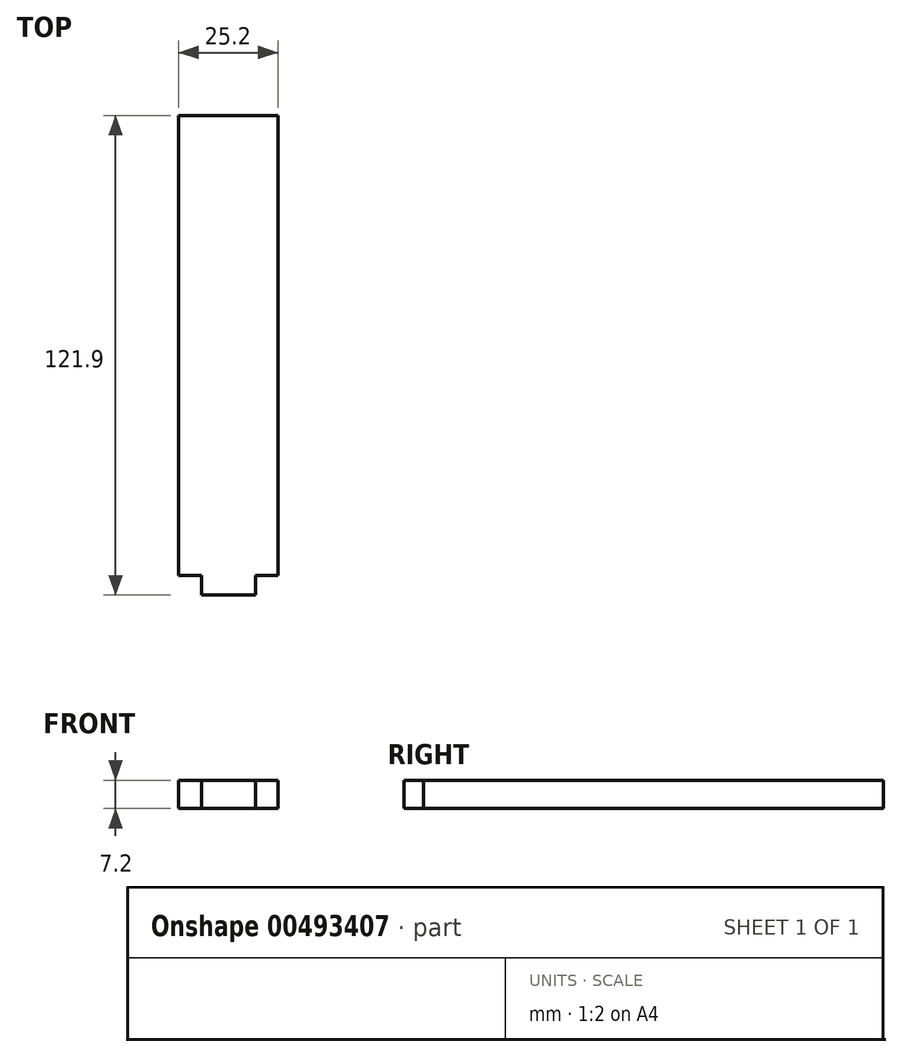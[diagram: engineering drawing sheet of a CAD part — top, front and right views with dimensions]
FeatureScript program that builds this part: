
annotation { "Feature Type Name" : "Feature", "Feature Type Description" : "" }
export const myFeature = defineFeature(function(context is Context, id is Id, definition is map)
    precondition{}
    {
        {
            var Q0;
            Q0=qCreatedBy(makeId("Front.planeOp"),FACE);
            var sketch = newSketch(context, id + "F0", { "sketchPlane" : qUnion([Q0])});
            skLineSegment(sketch, "E0.bottom", {"start": v(-19.14, 25.9) * mm, "end": v(6.06, 25.9) * mm});
            skLineSegment(sketch, "E0.top", {"start": v(-19.14, 18.7) * mm, "end": v(6.06, 18.7) * mm});
            skLineSegment(sketch, "E0.left", {"start": v(-19.14, 25.9) * mm, "end": v(-19.14, 18.7) * mm});
            skLineSegment(sketch, "E0.right", {"start": v(6.06, 25.9) * mm, "end": v(6.06, 18.7) * mm});
            skSolve(sketch);
        }
        {
            var Q0;
            Q0=makeQuery(id+"F0.imprint","IMPRINT",FACE,{"disambiguationData":[TD([[makeQuery(id+"F0.imprint","IMPRINT",EDGE,{"derivedFrom":sQuery(id+"F0.wireOp",EDGE,"E0.bottom")}),-1.0]])]});
            extrude(context, id + "F1", {"entities" : qUnion([Q0]), "endBound" : BoundingType.SYMMETRIC, "depth" : 116.9 * mm});
        }
        {
            var Q0;
            Q0=makeQuery(id+"F1.opExtrude","CAP_FACE",FACE,{"disambiguationData":[OSD([sQuery(id+"F0.wireOp",EDGE,"E0.bottom"),sQuery(id+"F0.wireOp",EDGE,"E0.top"),sQuery(id+"F0.wireOp",EDGE,"E0.left"),sQuery(id+"F0.wireOp",EDGE,"E0.right")])],"isStart":false});
            var sketch = newSketch(context, id + "F2", { "sketchPlane" : qUnion([Q0])});
            skLineSegment(sketch, "E1.bottom", {"start": v(-13.31, 18.7) * mm, "end": v(0.39, 18.7) * mm});
            skLineSegment(sketch, "E1.top", {"start": v(-13.31, 25.9) * mm, "end": v(0.39, 25.9) * mm});
            skLineSegment(sketch, "E1.left", {"start": v(-13.31, 18.7) * mm, "end": v(-13.31, 25.9) * mm});
            skLineSegment(sketch, "E1.right", {"start": v(0.39, 18.7) * mm, "end": v(0.39, 25.9) * mm});
            skSolve(sketch);
        }
        {
            var Q0;
            Q0 = qSketchRegion(id + "F2", true);
            extrude(context, id + "F3", {"entities" : qUnion([Q0]), "operationType" : NewBodyOperationType.ADD, "depth" : 5 * mm});
        }
    });
